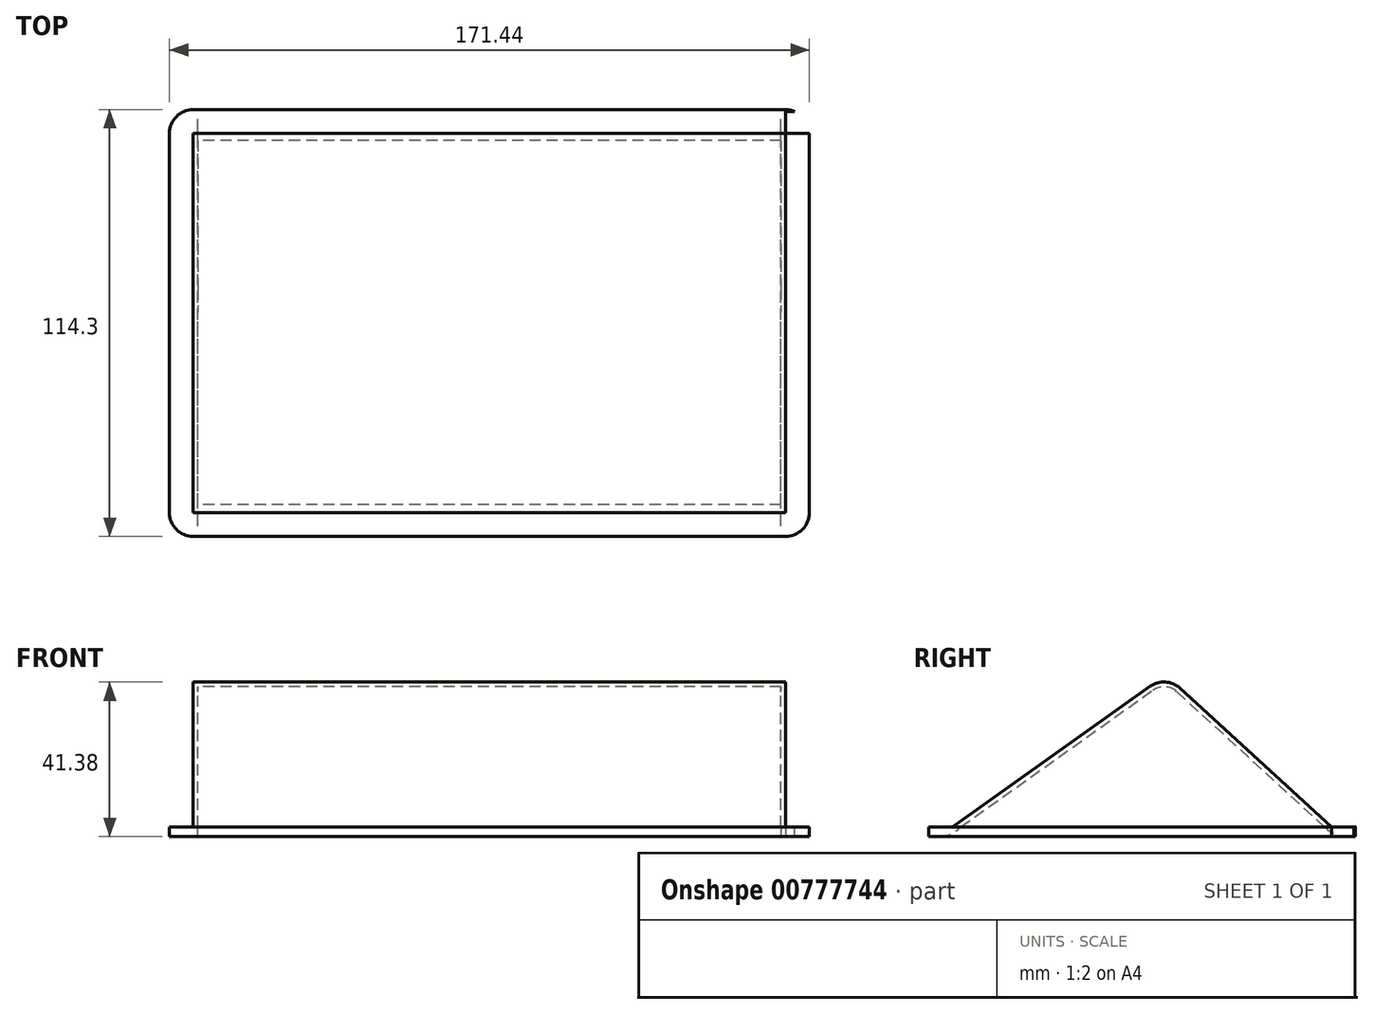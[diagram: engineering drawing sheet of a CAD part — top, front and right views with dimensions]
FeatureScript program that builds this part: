
annotation { "Feature Type Name" : "Feature", "Feature Type Description" : "" }
export const myFeature = defineFeature(function(context is Context, id is Id, definition is map)
    precondition{}
    {
        {
            var Q0;
            Q0=qCreatedBy(makeId("Right.planeOp"),FACE);
            var sketch = newSketch(context, id + "F0", { "sketchPlane" : qUnion([Q0])});
            skLineSegment(sketch, "E0", {"start": v(-48.67, 0) * mm, "end": v(52.93, 0) * mm});
            skPoint(sketch, "E1", {"position": v(8.48, 0) * mm});
            skPoint(sketch, "E2", {"position": v(8.48, 40.64) * mm});
            skLineSegment(sketch, "E3", {"start": v(-48.67, 0) * mm, "end": v(4.3, 37.67) * mm});
            skLineSegment(sketch, "E4", {"start": v(52.93, 0) * mm, "end": v(12.27, 37.18) * mm});
            skArc(sketch, "E5.filletArc", {"start": v(12.27, 37.18) * mm, "mid": v(8.37, 38.83) * mm, "end": v(4.3, 37.67) * mm});
            skSolve(sketch);
        }
        {
            var Q0;
            Q0=makeQuery(id+"F0.imprint","IMPRINT",FACE,{"disambiguationData":[TD([[makeQuery(id+"F0.imprint","IMPRINT",EDGE,{"derivedFrom":sQuery(id+"F0.wireOp",EDGE,"E0")}),1.0]])]});
            extrude(context, id + "F1", {"entities" : qUnion([Q0]), "endBound" : BoundingType.SYMMETRIC, "depth" : 158.75 * mm, "offsetDistance" : 25.4 * mm});
        }
        {
            var Q0;
            Q0=makeQuery(id+"F1.opExtrude","SWEPT_FACE",FACE,{"disambiguationData":[OSD([sQuery(id+"F0.wireOp",EDGE,"E0")])]});
            shell(context, id + "F2", {"entities" : qUnion([Q0]), "thickness" : 1.27 * mm});
        }
        {
            var Q0;
            Q0=makeQuery(id+"F1.opExtrude","SWEPT_FACE",FACE,{"disambiguationData":[OSD([sQuery(id+"F0.wireOp",EDGE,"E0")])]});
            var sketch = newSketch(context, id + "F3", { "sketchPlane" : qUnion([Q0])});
            skLineSegment(sketch, "E6.bottom", {"start": v(-79.38, 55.02) * mm, "end": v(79.38, 55.02) * mm});
            skLineSegment(sketch, "E6.top", {"start": v(-79.38, -59.28) * mm, "end": v(79.38, -59.28) * mm});
            skLineSegment(sketch, "E6.left", {"start": v(-85.72, 48.67) * mm, "end": v(-85.72, -52.93) * mm});
            skLineSegment(sketch, "E6.right", {"start": v(85.73, 48.67) * mm, "end": v(85.73, -52.93) * mm});
            skPoint(sketch, "E6.middle", {"position": v(0, -2.13) * mm});
            skPoint(sketch, "E7.visualSharp", {"position": v(-85.73, 55.02) * mm});
            skArc(sketch, "E7.filletArc", {"start": v(-79.38, 55.02) * mm, "mid": v(-83.87, 53.16) * mm, "end": v(-85.73, 48.67) * mm});
            skPoint(sketch, "E8.visualSharp", {"position": v(-85.72, -59.28) * mm});
            skArc(sketch, "E8.filletArc", {"start": v(-85.73, -52.93) * mm, "mid": v(-83.87, -57.42) * mm, "end": v(-79.38, -59.28) * mm});
            skPoint(sketch, "E9.visualSharp", {"position": v(85.73, -59.28) * mm});
            skArc(sketch, "E9.filletArc", {"start": v(79.38, -59.28) * mm, "mid": v(83.87, -57.42) * mm, "end": v(85.73, -52.93) * mm});
            skPoint(sketch, "E10.visualSharp", {"position": v(85.73, 55.02) * mm});
            skArc(sketch, "E10.filletArc", {"start": v(85.72, 48.67) * mm, "mid": v(83.87, 53.16) * mm, "end": v(79.38, 55.02) * mm});
            skLineSegment(sketch, "E11.0", {"start": v(-78.1, 46.47) * mm, "end": v(-78.1, -51.05) * mm});
            skLineSegment(sketch, "E12.0", {"start": v(78.1, 46.47) * mm, "end": v(-78.1, 46.47) * mm});
            skLineSegment(sketch, "E13.0", {"start": v(78.1, 46.47) * mm, "end": v(78.1, -51.05) * mm});
            skLineSegment(sketch, "E14.0", {"start": v(78.1, -51.05) * mm, "end": v(-78.1, -51.05) * mm});
            skSolve(sketch);
        }
        {
            var Q0;
            Q0 = qSketchRegion(id + "F3", true);
            extrude(context, id + "F4", {"entities" : qUnion([Q0]), "operationType" : NewBodyOperationType.ADD, "depth" : 2.54 * mm, "offsetDistance" : 25.4 * mm});
        }
        {
            var Q0;
            Q0=makeQuery(id+"F4.opExtrude","CAP_EDGE",EDGE,{"disambiguationData":[OSD([sQuery(id+"F3.wireOp",EDGE,"E12.0")])],"isStart":false});
            var Q1;
            Q1=makeQuery(id+"F4.opExtrude","CAP_EDGE",EDGE,{"disambiguationData":[OSD([sQuery(id+"F3.wireOp",EDGE,"E14.0")])],"isStart":false});
            fillet(context, id + "F5", {"entities" : qUnion([Q0, Q1]), "radius" : 7.62 * mm, "tangentPropagation" : true, "allowEdgeOverflow" : false});
        }
        {
            var Q0;
            Q0=makeQuery(id+"F4.opExtrude","CAP_FACE",FACE,{"disambiguationData":[OSD([sQuery(id+"F3.wireOp",EDGE,"E6.bottom"),sQuery(id+"F3.wireOp",EDGE,"E6.top"),sQuery(id+"F3.wireOp",EDGE,"E6.left"),sQuery(id+"F3.wireOp",EDGE,"E6.right"),sQuery(id+"F3.wireOp",EDGE,"E7.filletArc"),sQuery(id+"F3.wireOp",EDGE,"E8.filletArc"),sQuery(id+"F3.wireOp",EDGE,"E9.filletArc"),sQuery(id+"F3.wireOp",EDGE,"E10.filletArc"),sQuery(id+"F3.wireOp",EDGE,"E11.0"),sQuery(id+"F3.wireOp",EDGE,"E12.0"),sQuery(id+"F3.wireOp",EDGE,"E13.0"),sQuery(id+"F3.wireOp",EDGE,"E14.0")])],"isStart":false});
            var sketch = newSketch(context, id + "F6", { "sketchPlane" : qUnion([Q0])});
            skLineSegment(sketch, "E15.bottom", {"start": v(106.6, -58.84) * mm, "end": v(79.38, -58.84) * mm});
            skLineSegment(sketch, "E15.top", {"start": v(106.6, -52.93) * mm, "end": v(79.38, -52.93) * mm});
            skLineSegment(sketch, "E15.left", {"start": v(106.6, -58.84) * mm, "end": v(106.6, -52.93) * mm});
            skLineSegment(sketch, "E15.right", {"start": v(79.38, -58.84) * mm, "end": v(79.38, -52.93) * mm});
            skSolve(sketch);
        }
        {
            var Q0;
            Q0 = qSketchRegion(id + "F6", true);
            extrude(context, id + "F7", {"entities" : qUnion([Q0]), "operationType" : NewBodyOperationType.REMOVE, "oppositeDirection" : true, "depth" : 25.4 * mm, "offsetDistance" : 25.4 * mm});
        }
    });
